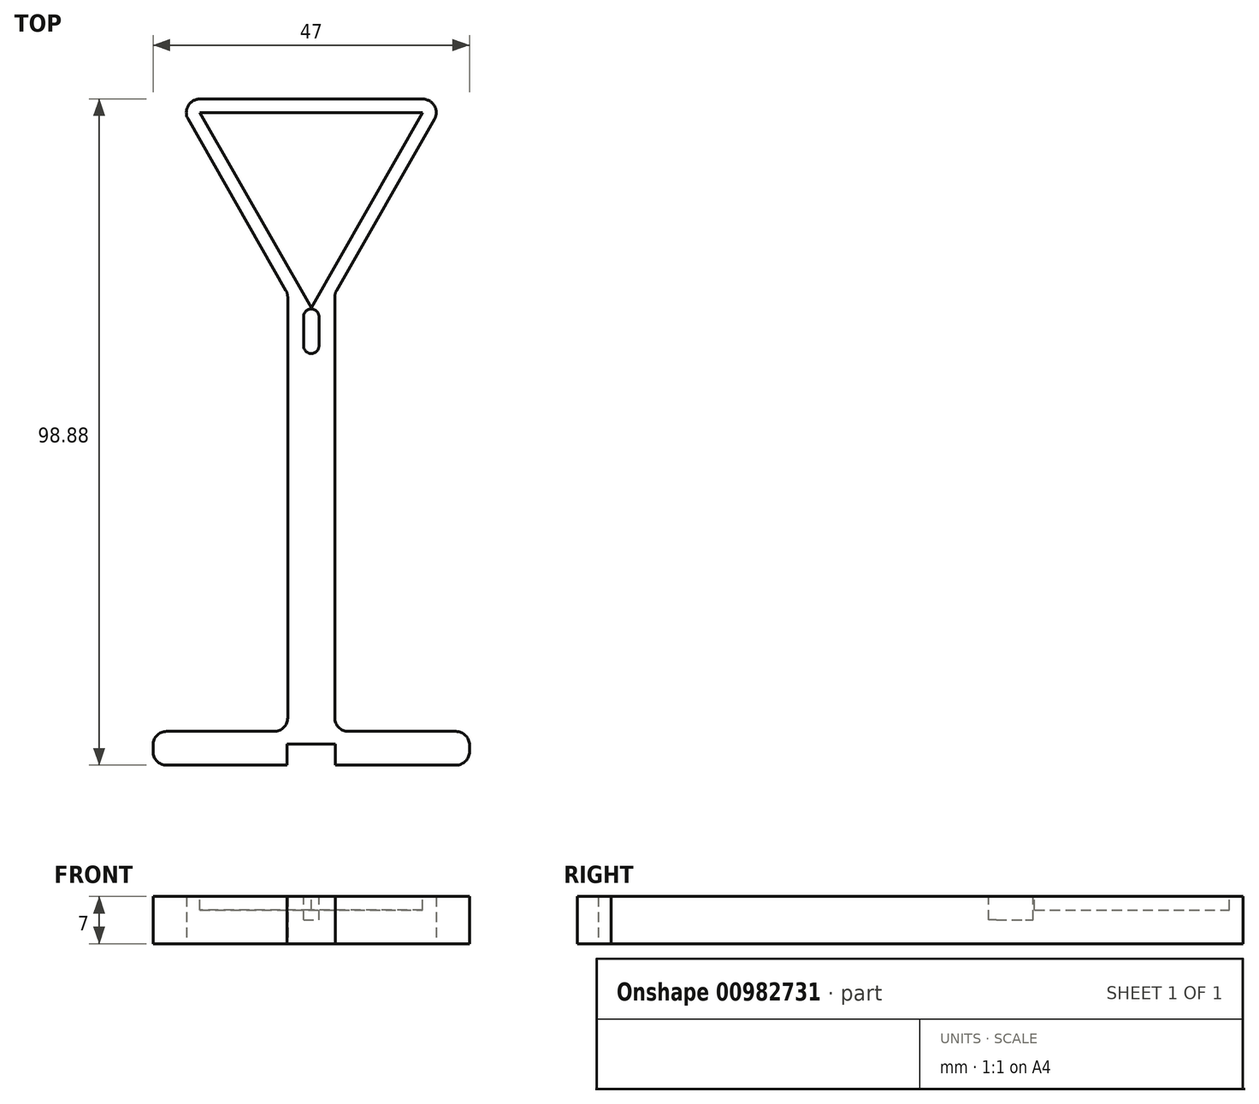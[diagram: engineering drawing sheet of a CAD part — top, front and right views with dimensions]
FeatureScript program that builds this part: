
annotation { "Feature Type Name" : "Feature", "Feature Type Description" : "" }
export const myFeature = defineFeature(function(context is Context, id is Id, definition is map)
    precondition{}
    {
        {
            var Q0;
            Q0=qCreatedBy(makeId("Top.planeOp"),FACE);
            var sketch = newSketch(context, id + "F0", { "sketchPlane" : qUnion([Q0])});
            skLineSegment(sketch, "E0", {"start": v(-3.5, -0.87) * mm, "end": v(-3.5, -65.88) * mm});
            skLineSegment(sketch, "E1", {"start": v(-3.5, -65.88) * mm, "end": v(-23.5, -65.88) * mm});
            skLineSegment(sketch, "E2", {"start": v(-23.5, -65.88) * mm, "end": v(-23.5, -70.88) * mm});
            skLineSegment(sketch, "E3", {"start": v(-23.5, -70.88) * mm, "end": v(23.5, -70.88) * mm});
            skLineSegment(sketch, "E4", {"start": v(23.5, -70.88) * mm, "end": v(23.5, -65.88) * mm});
            skLineSegment(sketch, "E5", {"start": v(23.5, -65.88) * mm, "end": v(3.5, -65.88) * mm});
            skLineSegment(sketch, "E6", {"start": v(3.5, -65.88) * mm, "end": v(3.5, -0.87) * mm});
            skLineSegment(sketch, "E7.bottom", {"start": v(3.6, -70.88) * mm, "end": v(-3.6, -70.88) * mm});
            skLineSegment(sketch, "E7.top", {"start": v(3.6, -67.78) * mm, "end": v(-3.6, -67.78) * mm});
            skLineSegment(sketch, "E7.left", {"start": v(3.6, -70.88) * mm, "end": v(3.6, -67.78) * mm});
            skLineSegment(sketch, "E7.right", {"start": v(-3.6, -70.88) * mm, "end": v(-3.6, -67.78) * mm});
            skPoint(sketch, "E7.middle", {"position": v(0, -69.33) * mm});
            skLineSegment(sketch, "E8.bottom", {"start": v(-23.5, -70.88) * mm, "end": v(-17.5, -70.88) * mm});
            skLineSegment(sketch, "E8.top", {"start": v(-23.5, -71.17) * mm, "end": v(-17.5, -71.17) * mm});
            skLineSegment(sketch, "E8.left", {"start": v(-23.5, -70.88) * mm, "end": v(-23.5, -71.17) * mm});
            skLineSegment(sketch, "E8.right", {"start": v(-17.5, -70.88) * mm, "end": v(-17.5, -71.17) * mm});
            skLineSegment(sketch, "E9.MirrorCS", {"start": v(23.5, -70.88) * mm, "end": v(17.5, -70.88) * mm});
            skLineSegment(sketch, "E10.MirrorCS", {"start": v(17.5, -70.88) * mm, "end": v(17.5, -71.17) * mm});
            skLineSegment(sketch, "E11.MirrorCS", {"start": v(23.5, -71.17) * mm, "end": v(17.5, -71.17) * mm});
            skLineSegment(sketch, "E12.MirrorCS", {"start": v(23.5, -70.88) * mm, "end": v(23.5, -71.17) * mm});
            skLineSegment(sketch, "E13", {"start": v(0, -7) * mm, "end": v(-20, 28) * mm});
            skLineSegment(sketch, "E14", {"start": v(-20, 28) * mm, "end": v(20, 28) * mm});
            skLineSegment(sketch, "E15", {"start": v(20, 28) * mm, "end": v(0, -7) * mm});
            skSolve(sketch);
        }
        {
            var Q0;
            {var subQ0=sQuery(id+"F0.wireOp",EDGE,"im0v1Rov-prSM-cwdN-f0IW-ScqFdnQkXUSi");Q0=makeQuery(id+"F0.imprint","IMPRINT",FACE,{"disambiguationData":[TD([[makeQuery(id+"F0.imprint","IMPRINT",EDGE,{"derivedFrom":subQ0}),1.0]])]});}
            var Q1;
            {var subQ7=sQuery(id+"F0.wireOp",EDGE,"E0");Q1=makeQuery(id+"F0.imprint","IMPRINT",FACE,{"disambiguationData":[TD([[makeQuery(id+"F0.imprint","IMPRINT",EDGE,{"derivedFrom":subQ7}),1.0]])]});}
            var Q2;
            Q2=makeQuery(id+"F0.imprint","IMPRINT",FACE,{"disambiguationData":[TD([[makeQuery(id+"F0.imprint","IMPRINT",EDGE,{"derivedFrom":sQuery(id+"F0.wireOp",EDGE,"E8.bottom")}),-1.0]])]});
            var Q3;
            Q3=makeQuery(id+"F0.imprint","IMPRINT",FACE,{"disambiguationData":[TD([[makeQuery(id+"F0.imprint","IMPRINT",EDGE,{"derivedFrom":sQuery(id+"F0.wireOp",EDGE,"E9.MirrorCS")}),1.0]])]});
            var Q4;
            {var subQ2=sQuery(id+"F0.wireOp",EDGE,"E14");Q4=makeQuery(id+"F0.imprint","IMPRINT",FACE,{"disambiguationData":[TD([[makeQuery(id+"F0.imprint","IMPRINT",EDGE,{"derivedFrom":subQ2}),-1.0]])]});}
            extrude(context, id + "F1", {"entities" : qUnion([Q0, Q1, Q2, Q3, Q4]), "depth" : 7 * mm, "offsetDistance" : 25 * mm});
        }
        {
            var Q0;
            Q0=makeQuery(id+"F1.opExtrude","CAP_FACE",FACE,{"disambiguationData":[OSD([sQuery(id+"F0.wireOp",EDGE,"E0"),sQuery(id+"F0.wireOp",EDGE,"E1"),sQuery(id+"F0.wireOp",EDGE,"E2"),sQuery(id+"F0.wireOp",EDGE,"E3"),sQuery(id+"F0.wireOp",EDGE,"E4"),sQuery(id+"F0.wireOp",EDGE,"E5"),sQuery(id+"F0.wireOp",EDGE,"E6"),sQuery(id+"F0.wireOp",EDGE,"E7.top"),sQuery(id+"F0.wireOp",EDGE,"E7.left"),sQuery(id+"F0.wireOp",EDGE,"E7.right"),sQuery(id+"F0.wireOp",EDGE,"E8.top"),sQuery(id+"F0.wireOp",EDGE,"E8.left"),sQuery(id+"F0.wireOp",EDGE,"E8.right"),sQuery(id+"F0.wireOp",EDGE,"E10.MirrorCS"),sQuery(id+"F0.wireOp",EDGE,"E11.MirrorCS"),sQuery(id+"F0.wireOp",EDGE,"E12.MirrorCS"),sQuery(id+"F0.wireOp",EDGE,"E13"),sQuery(id+"F0.wireOp",EDGE,"E14"),sQuery(id+"F0.wireOp",EDGE,"E15")])],"isStart":false});
            var sketch = newSketch(context, id + "F2", { "sketchPlane" : qUnion([Q0])});
            skLineSegment(sketch, "E16", {"start": v(-16.55, 26) * mm, "end": v(16.55, 26) * mm});
            skLineSegment(sketch, "E17", {"start": v(16.55, 26) * mm, "end": v(0, -2.97) * mm});
            skLineSegment(sketch, "E18", {"start": v(0, -2.97) * mm, "end": v(-16.55, 26) * mm});
            skSolve(sketch);
        }
        {
            var Q0;
            Q0=makeQuery(id+"F2.imprint","IMPRINT",FACE,{"disambiguationData":[TD([[makeQuery(id+"F2.imprint","IMPRINT",EDGE,{"derivedFrom":sQuery(id+"F2.wireOp",EDGE,"E16")}),-1.0]])]});
            extrude(context, id + "F3", {"entities" : qUnion([Q0]), "operationType" : NewBodyOperationType.REMOVE, "oppositeDirection" : true, "depth" : 2 * mm, "offsetDistance" : 25 * mm});
        }
        {
            var Q0;
            Q0=makeQuery(id+"F1.opExtrude","SWEPT_EDGE",EDGE,{"disambiguationData":[OSD([sQuery(id+"F0.wireOp",EDGE,"0U4RxweM-u2bA-2Qqt-OOBg-x1ftkZs6jUrD"),sQuery(id+"F0.wireOp",EDGE,"E0")])]});
            var Q1;
            Q1=makeQuery(id+"F1.opExtrude","SWEPT_EDGE",EDGE,{"disambiguationData":[OSD([sQuery(id+"F0.wireOp",EDGE,"0U4RxweM-u2bA-2Qqt-OOBg-x1ftkZs6jUrD"),sQuery(id+"F0.wireOp",EDGE,"E6")])]});
            var Q2;
            Q2=makeQuery(id+"F1.opExtrude","SWEPT_EDGE",EDGE,{"disambiguationData":[OSD([sQuery(id+"F0.wireOp",EDGE,"0U4RxweM-u2bA-2Qqt-OOBg-x1ftkZs6jUrD"),sQuery(id+"F0.wireOp",EDGE,"im0v1Rov-prSM-cwdN-f0IW-ScqFdnQkXUSi")])]});
            var Q3;
            Q3=makeQuery(id+"F1.opExtrude","SWEPT_EDGE",EDGE,{"disambiguationData":[OSD([sQuery(id+"F0.wireOp",EDGE,"0U4RxweM-u2bA-2Qqt-OOBg-x1ftkZs6jUrD"),sQuery(id+"F0.wireOp",EDGE,"IfBi3EXo-PReU-dRJG-joro-0UU4bWJMkuGZ")])]});
            var Q4;
            Q4=makeQuery(id+"F1.opExtrude","SWEPT_EDGE",EDGE,{"disambiguationData":[OSD([sQuery(id+"F0.wireOp",EDGE,"im0v1Rov-prSM-cwdN-f0IW-ScqFdnQkXUSi"),sQuery(id+"F0.wireOp",EDGE,"IfBi3EXo-PReU-dRJG-joro-0UU4bWJMkuGZ")])]});
            var Q5;
            Q5=makeQuery(id+"F1.opExtrude","SWEPT_EDGE",EDGE,{"disambiguationData":[OSD([sQuery(id+"F0.wireOp",EDGE,"E5"),sQuery(id+"F0.wireOp",EDGE,"E6")])]});
            var Q6;
            Q6=makeQuery(id+"F1.opExtrude","SWEPT_EDGE",EDGE,{"disambiguationData":[OSD([sQuery(id+"F0.wireOp",EDGE,"E0"),sQuery(id+"F0.wireOp",EDGE,"E1")])]});
            var Q7;
            Q7=makeQuery(id+"F1.opExtrude","SWEPT_EDGE",EDGE,{"disambiguationData":[OSD([sQuery(id+"F0.wireOp",EDGE,"E1"),sQuery(id+"F0.wireOp",EDGE,"E2")])]});
            var Q8;
            Q8=makeQuery(id+"F1.opExtrude","SWEPT_EDGE",EDGE,{"disambiguationData":[OSD([sQuery(id+"F0.wireOp",EDGE,"E4"),sQuery(id+"F0.wireOp",EDGE,"E5")])]});
            var Q9;
            Q9=makeQuery(id+"F1.opExtrude","SWEPT_EDGE",EDGE,{"disambiguationData":[OSD([sQuery(id+"F0.wireOp",EDGE,"E8.top"),sQuery(id+"F0.wireOp",EDGE,"E8.left")])]});
            var Q10;
            Q10=makeQuery(id+"F1.opExtrude","SWEPT_EDGE",EDGE,{"disambiguationData":[OSD([sQuery(id+"F0.wireOp",EDGE,"E11.MirrorCS"),sQuery(id+"F0.wireOp",EDGE,"E12.MirrorCS")])]});
            var Q11;
            Q11=makeQuery(id+"F1.opExtrude","SWEPT_EDGE",EDGE,{"disambiguationData":[OSD([sQuery(id+"F0.wireOp",EDGE,"E13"),sQuery(id+"F0.wireOp",EDGE,"E14")])]});
            var Q12;
            Q12=makeQuery(id+"F1.opExtrude","SWEPT_EDGE",EDGE,{"disambiguationData":[OSD([sQuery(id+"F0.wireOp",EDGE,"E14"),sQuery(id+"F0.wireOp",EDGE,"E15")])]});
            fillet(context, id + "F4", {"entities" : qUnion([Q0, Q1, Q2, Q3, Q4, Q5, Q6, Q7, Q8, Q9, Q10, Q11, Q12]), "radius" : 2 * mm, "tangentPropagation" : true, "allowEdgeOverflow" : false});
        }
        {
            var Q0;
            Q0=makeQuery(id+"F1.opExtrude","CAP_FACE",FACE,{"disambiguationData":[OSD([sQuery(id+"F0.wireOp",EDGE,"E0"),sQuery(id+"F0.wireOp",EDGE,"E1"),sQuery(id+"F0.wireOp",EDGE,"E2"),sQuery(id+"F0.wireOp",EDGE,"E3"),sQuery(id+"F0.wireOp",EDGE,"E4"),sQuery(id+"F0.wireOp",EDGE,"E5"),sQuery(id+"F0.wireOp",EDGE,"E6"),sQuery(id+"F0.wireOp",EDGE,"E7.top"),sQuery(id+"F0.wireOp",EDGE,"E7.left"),sQuery(id+"F0.wireOp",EDGE,"E7.right"),sQuery(id+"F0.wireOp",EDGE,"E8.top"),sQuery(id+"F0.wireOp",EDGE,"E8.left"),sQuery(id+"F0.wireOp",EDGE,"E8.right"),sQuery(id+"F0.wireOp",EDGE,"E10.MirrorCS"),sQuery(id+"F0.wireOp",EDGE,"E11.MirrorCS"),sQuery(id+"F0.wireOp",EDGE,"E12.MirrorCS"),sQuery(id+"F0.wireOp",EDGE,"E13"),sQuery(id+"F0.wireOp",EDGE,"E14"),sQuery(id+"F0.wireOp",EDGE,"E15")])],"isStart":false});
            var sketch = newSketch(context, id + "F5", { "sketchPlane" : qUnion([Q0])});
            skLineSegment(sketch, "E19.bottom", {"start": v(1.15, -8.62) * mm, "end": v(-1.15, -8.62) * mm});
            skLineSegment(sketch, "E19.top", {"start": v(1.15, -4.32) * mm, "end": v(-1.15, -4.32) * mm});
            skLineSegment(sketch, "E19.left", {"start": v(1.15, -8.62) * mm, "end": v(1.15, -4.32) * mm});
            skLineSegment(sketch, "E19.right", {"start": v(-1.15, -8.62) * mm, "end": v(-1.15, -4.32) * mm});
            skPoint(sketch, "E19.middle", {"position": v(0, -6.47) * mm});
            skArc(sketch, "E20", {"start": v(-1.15, -4.32) * mm, "mid": v(0, -3.17) * mm, "end": v(1.15, -4.32) * mm});
            skArc(sketch, "E21", {"start": v(-1.15, -8.62) * mm, "mid": v(0, -9.77) * mm, "end": v(1.15, -8.62) * mm});
            skSolve(sketch);
        }
        {
            var Q0;
            Q0=makeQuery(id+"F5.imprint","IMPRINT",FACE,{"disambiguationData":[TD([[makeQuery(id+"F5.imprint","IMPRINT",EDGE,{"derivedFrom":sQuery(id+"F5.wireOp",EDGE,"E19.bottom")}),1.0]])]});
            var Q1;
            Q1=makeQuery(id+"F5.imprint","IMPRINT",FACE,{"disambiguationData":[TD([[makeQuery(id+"F5.imprint","IMPRINT",EDGE,{"derivedFrom":sQuery(id+"F5.wireOp",EDGE,"E19.bottom")}),-1.0]])]});
            var Q2;
            Q2=makeQuery(id+"F5.imprint","IMPRINT",FACE,{"disambiguationData":[TD([[makeQuery(id+"F5.imprint","IMPRINT",EDGE,{"derivedFrom":sQuery(id+"F5.wireOp",EDGE,"E19.top")}),-1.0]])]});
            extrude(context, id + "F6", {"entities" : qUnion([Q0, Q1, Q2]), "operationType" : NewBodyOperationType.REMOVE, "oppositeDirection" : true, "depth" : 3.5 * mm, "offsetDistance" : 25 * mm});
        }
    });
